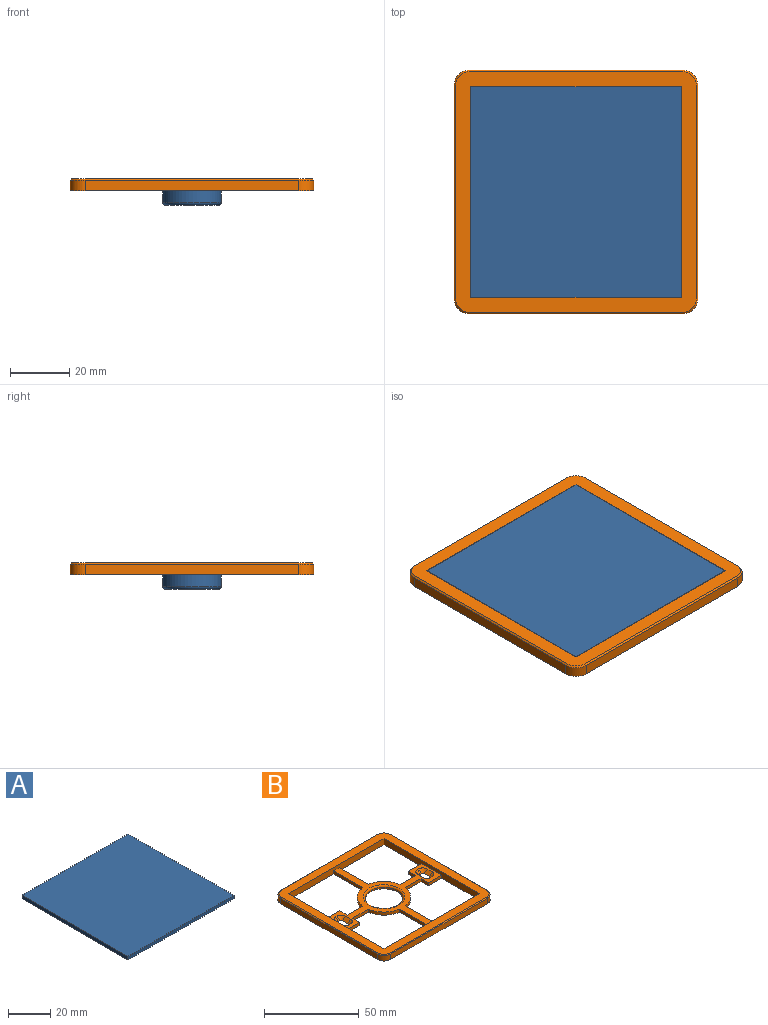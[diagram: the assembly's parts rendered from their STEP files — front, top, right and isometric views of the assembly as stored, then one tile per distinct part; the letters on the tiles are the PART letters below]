
ASSEMBLY  parts=2 mates=1
PART A: 9 faces, bbox 70.8x70.8x9 mm
  f0: plane 70.8x2mm, normal (1,0,0), area 141.6mm2, adj f1,f3,f4,f5
  f1: plane 70.8x2mm, normal (0,1,0), area 141.6mm2, adj f0,f2,f4,f5
  f2: plane 70.8x2mm, normal (-1,0,0), area 141.6mm2, adj f1,f3,f4,f5
  f3: plane 70.8x2mm, normal (0,-1,0), area 141.6mm2, adj f0,f2,f4,f5
  f4: plane 70.8x70.8mm, normal (0,0,1), area 5012.6mm2, adj f0,f1,f2,f3
  f5: plane 70.8x70.8mm, normal (0,0,-1), area 4704.7mm2, adj f0,f1,f2,f3,f6
  f6: cylinder r=9.9mm len=19.8mm, axis (0,0,1), area 373.2mm2, adj f5,f8
  f7: plane 17.8x17.8mm, normal (0,0,-1), area 248.8mm2, adj f8
  f8: torus R=8.9mm, axis (0,0,-1), area 94.1mm2, adj f6,f7
PART B: 61 faces, bbox 82x82x4 mm
  f0: plane 71x4mm, normal (0,-1,0), area 276mm2, adj f3,f4,f5,f10,f24,f53,f54
  f1: plane 5.37x2mm, normal (1,0,0), area 10.7mm2, adj f5,f24,f25,f50
  f2: plane 5.37x2mm, normal (-1,0,0), area 10.7mm2, adj f5,f24,f28,f57
  f3: plane 71x4mm, normal (1,0,0), area 254mm2, adj f0,f4,f5,f11,f24,f25,f26
  f4: plane 81x81mm, normal (0,0,1), area 1502.6mm2, adj f0,f3,f10,f11,f16,f17,f18,f19
  f5: plane 82x82mm, normal (0,0,-1), area 2492.1mm2, adj f0,f1,f2,f3,f6,f7,f8,f9
  f6: plane 72x3.5mm, normal (1,0,0), area 252mm2, adj f5,f12,f15,f16
  f7: plane 72x3.5mm, normal (0,1,0), area 252mm2, adj f5,f12,f13,f19
  f8: plane 72x3.5mm, normal (-1,0,0), area 252mm2, adj f5,f13,f14,f23
  f9: plane 72x3.5mm, normal (0,-1,0), area 252mm2, adj f5,f14,f15,f20
  f10: plane 71x4mm, normal (-1,0,0), area 254mm2, adj f0,f4,f5,f11,f24,f28,f30
  f11: plane 71x4mm, normal (0,1,0), area 276mm2, adj f3,f4,f5,f10,f24,f47,f48
  f12: cylinder r=5mm len=5mm, axis (0,0,1), area 27.5mm2, adj f5,f6,f7,f17
  f13: cylinder r=5mm len=5mm, axis (0,0,-1), area 27.5mm2, adj f5,f7,f8,f21
  f14: cylinder r=5mm len=5mm, axis (0,0,1), area 27.5mm2, adj f5,f8,f9,f22
  f15: cylinder r=5mm len=5mm, axis (0,0,-1), area 27.5mm2, adj f5,f6,f9,f18
  f16: plane 72x0.5mm, normal (0.71,0,0.71), area 50.9mm2, adj f4,f6,f17,f18
  f17: cone r=4.5mm half-angle=45deg, axis (0,0,-1), area 5.3mm2, adj f4,f12,f16,f19
  f18: cone r=4.5mm half-angle=45deg, axis (0,0,-1), area 5.3mm2, adj f4,f15,f16,f20
  f19: plane 72x0.5mm, normal (0,0.71,0.71), area 50.9mm2, adj f4,f7,f17,f21
  f20: plane 72x0.5mm, normal (0,-0.71,0.71), area 50.9mm2, adj f4,f9,f18,f22
  f21: cone r=4.5mm half-angle=45deg, axis (0,0,-1), area 5.3mm2, adj f4,f13,f19,f23
  f22: cone r=4.5mm half-angle=45deg, axis (0,0,-1), area 5.3mm2, adj f4,f14,f20,f23
  f23: plane 72x0.5mm, normal (-0.71,0,0.71), area 50.9mm2, adj f4,f8,f21,f22
  f24: plane 71x71mm, normal (0,0,1), area 674.3mm2, adj f0,f1,f2,f3,f10,f11,f25,f26
  f25: plane 10x2mm, normal (0,-1,0), area 20mm2, adj f1,f3,f5,f24
  f26: plane 10x2mm, normal (0,1,0), area 20mm2, adj f3,f5,f24,f27
  f27: plane 5.63x2mm, normal (1,0,0), area 11.3mm2, adj f5,f24,f26,f51
  f28: plane 10x2mm, normal (0,-1,0), area 20mm2, adj f2,f5,f10,f24
  f29: plane 5.63x2mm, normal (-1,0,0), area 11.3mm2, adj f5,f24,f30,f56
  f30: plane 10x2mm, normal (0,1,0), area 20mm2, adj f5,f10,f24,f29
  f31: plane 4x2mm, normal (-0.71,0,0.71), area 11.3mm2, adj f5,f24,f32,f33
  f32: cone r=3mm half-angle=45deg, axis (0,0,1), area 8.9mm2, adj f5,f24,f31,f34
  f33: cone r=3mm half-angle=45deg, axis (0,0,1), area 8.9mm2, adj f5,f24,f31,f35
  f34: plane 2x2mm, normal (0,-0.71,0.71), area 2.8mm2, adj f5,f24,f32,f36
  f35: plane 2x2mm, normal (0,0.71,0.71), area 2.8mm2, adj f5,f24,f33,f37
  f36: cone r=3mm half-angle=45deg, axis (0,0,1), area 8.9mm2, adj f5,f24,f34,f38
  f37: cone r=3mm half-angle=45deg, axis (0,0,1), area 8.9mm2, adj f5,f24,f35,f38
  f38: plane 4x2mm, normal (0.71,0,0.71), area 11.3mm2, adj f5,f24,f36,f37
  f39: cone r=3mm half-angle=45deg, axis (0,0,1), area 8.9mm2, adj f5,f24,f40,f41
  f40: plane 4x2mm, normal (-0.71,0,0.71), area 11.3mm2, adj f5,f24,f39,f42
  f41: plane 2x2mm, normal (0,-0.71,0.71), area 2.8mm2, adj f5,f24,f39,f43
  f42: cone r=3mm half-angle=45deg, axis (0,0,1), area 8.9mm2, adj f5,f24,f40,f44
  f43: cone r=3mm half-angle=45deg, axis (0,0,1), area 8.9mm2, adj f5,f24,f41,f45
  f44: plane 2x2mm, normal (0,0.71,0.71), area 2.8mm2, adj f5,f24,f42,f46
  f45: plane 4x2mm, normal (0.71,0,0.71), area 11.3mm2, adj f5,f24,f43,f46
  f46: cone r=3mm half-angle=45deg, axis (0,0,1), area 8.9mm2, adj f5,f24,f44,f45
  f47: plane 21.64x2mm, normal (1,0,0), area 43.3mm2, adj f5,f11,f24,f58
  f48: plane 21.64x2mm, normal (-1,0,0), area 43.3mm2, adj f5,f11,f24,f49
  f49: cylinder r=14mm len=11.84mm, axis (0,0,-1), area 35.7mm2, adj f5,f24,f48,f50
  f50: plane 11.66x2mm, normal (0,-1,0), area 23.3mm2, adj f1,f5,f24,f49
  f51: plane 11.63x2mm, normal (0,1,0), area 23.3mm2, adj f5,f24,f27,f52
  f52: cylinder r=14mm len=11.99mm, axis (0,0,-1), area 36.2mm2, adj f5,f24,f51,f53
  f53: plane 21.64x2mm, normal (-1,0,0), area 43.3mm2, adj f0,f5,f24,f52
  f54: plane 21.64x2mm, normal (1,0,0), area 43.3mm2, adj f0,f5,f24,f55
  f55: cylinder r=14mm len=11.99mm, axis (0,0,-1), area 36.2mm2, adj f5,f24,f54,f56
  f56: plane 11.63x2mm, normal (0,1,0), area 23.3mm2, adj f5,f24,f29,f55
  f57: plane 11.63x2mm, normal (-0.02,-1,0), area 23.3mm2, adj f2,f5,f24,f58
  f58: cylinder r=14mm len=11.99mm, axis (0,0,-1), area 36.2mm2, adj f5,f24,f47,f57
  f59: cylinder r=10mm len=20mm, axis (0,0,-1), area 62.8mm2, adj f5,f60
  f60: torus R=11mm, axis (0,0,-1), area 102.3mm2, adj f24,f59
PLACE A t=(-30.94,-6.94,-47.45)mm
PLACE B t=(-30.94,-6.94,-49.45)mm
MATE fastened A.f6 <-> B.f59  axis (0,0,1) through (-30.94,-6.94,-45.45)mm
